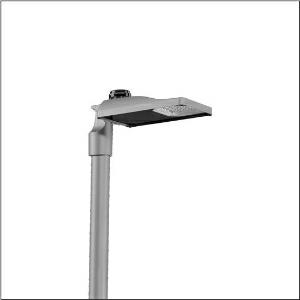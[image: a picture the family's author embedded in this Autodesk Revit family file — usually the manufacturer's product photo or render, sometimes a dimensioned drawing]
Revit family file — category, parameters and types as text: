
# Revit family: streetlight_sl_31_micro___p1_0a_5xh5a75n08da_cf7a
name_source: partatom
category: Lighting Fixtures
units: mm (PartAtom-declared; Revit-internal decimal feet)

## family parameters
Cut with Voids When Loaded = No
Host = Face
Light Source = No
Part Type = Normal
Room Calculation Point = No
Round Connector Dimension = Use Diameter
Shared = No

## types (1)
- --- (1 x LED, 3700 lm, 35.5 W, 2200K)
    Apparent Load = 36 VA
    CIE Flux Codes = 23 55 94 100 100
    Color Rendering = 70
    Color Temperature = 2200K
    Default Elevation = 1800 mm
    Description = Streetlight SL 31 micro NEMA (7pin), Desk-Remote mast luminaire for post-top, side-entry; light control with lens of PMMA; light distribution: P1.0a, direct asymmetric distribution, for standard-compliant lighting for roads and squares; LED: luminous flux: 3.700lm, light colour: 722, colour temperature: 2200K; luminous efficacy: 104,2lm/W; control: pre-setting: linear dimming characteristic, flexible luminous flux parameterisation, time-dependent luminous flux control, constant luminous flux control, intelligent temperature release in ECG and LED module, overheat protection; luminaire housing, of diecast aluminium, SITECO metallic grey (DB 702S), corrosivity category C5 high according to DIN EN ISO 12944; cover of toughened safety glass, transparent, opened without tools; mast flange of diecast aluminium, SITECO metallic grey (DB 702S), spigot size: 76/60mm, mast flange included unmounted; cable length: 6,5m, connection cable pre-assembled; mains connection: 220..240V, AC, 50/60Hz; power consumption (at start of service life): 35,5W / (at end of service life): 37,5W / (with reduced operation 50%): 15,4W; protection rating (complete): IP66; insulation class (complete): insulation class I (protective earthing); impact resistance: IK10; certification: CE, ENEC, ENEC+, VDE, UKCA; permissible operating ambient temperature for outdoor applications: -40..+50°C; packaging unit: 1 piece

Light Distribution: P1.0a
    Height = 76 mm
    Lamp = 1 x LED
    Lamp Light Flux = 3700 lm
    Lamp Power = 35.5 W
    Lamp count = 1
    Length = 467 mm
    Luminous efficacy = 104 lm/W
    Manufacturer = Siteco
    ModVariant = No
    Model = 5XH5A75N08DA
    Number of Poles = 1
    OnlyDefault = Yes
    Power Factor = 1
    Product Name = Streetlight SL 31 micro | P1.0a
    Product group = mast luminaire | pylon top
    ProductGroupID = 6100
    Protection Class = Protection class I
    Protection Degree = IP 66
    RLX_Detail_Level = 1
    RLX_Emergency_Light_Flux = 0 lm
    RLX_Emergency_Type = 0
    RLX_Emergency_Type_DB = No
    RlxData = <blob elided: 23401 chars, md5=88721a97>
    Socket = socket
    Standby Power = 0 W
    System Light Flux = 3700 lm
    System Power = 36 W
    Type Comments = factory setting: luminous flux: 100 % | dim-lin: 254 | 700 mA
    Type Image = l_1300305.jpg
    URL = http://relux.com
    VarID = @adj_015405
    Voltage = 0 V
    Weight = 0.00 kg
    Width = 265 mm

## geometry (parser evidence)
native form markers: Blend x4, Sweep x11
no freeform markers — native parametric forms only
